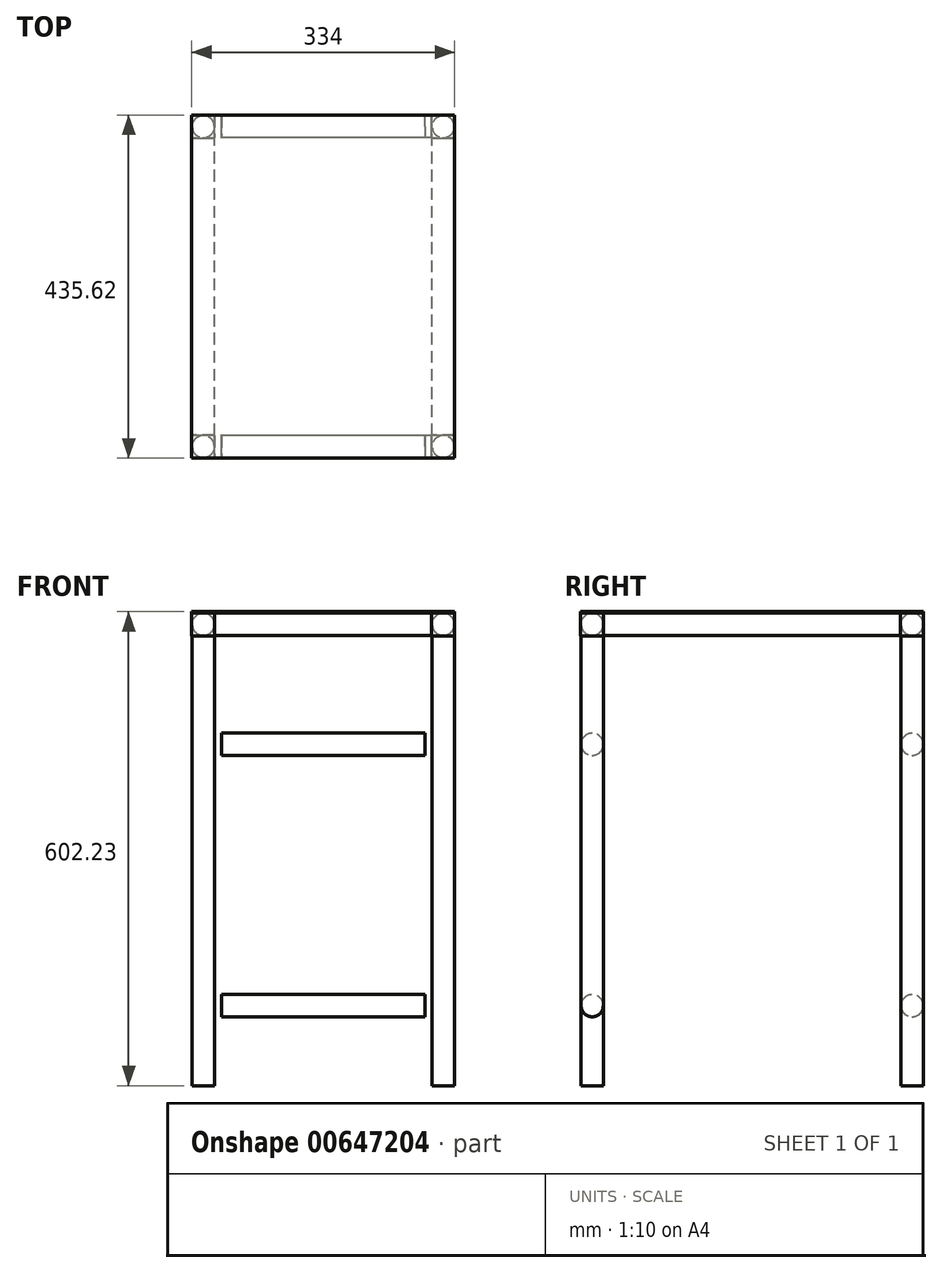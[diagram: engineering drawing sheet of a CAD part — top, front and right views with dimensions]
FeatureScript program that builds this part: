
annotation { "Feature Type Name" : "Feature", "Feature Type Description" : "" }
export const myFeature = defineFeature(function(context is Context, id is Id, definition is map)
    precondition{}
    {
        {
            var Q0;
            Q0=qCreatedBy(makeId("Top.planeOp"),FACE);
            var sketch = newSketch(context, id + "F0", { "sketchPlane" : qUnion([Q0])});
            skCircle(sketch, "E0", {"center": v(-152.4, 203.2) * mm, "radius": 14.05 * mm});
            skCircle(sketch, "E1", {"center": v(152.4, 203.2) * mm, "radius": 14.05 * mm});
            skCircle(sketch, "E2", {"center": v(-152.4, -203.2) * mm, "radius": 14.05 * mm});
            skCircle(sketch, "E3", {"center": v(152.4, -203.2) * mm, "radius": 14.05 * mm});
            skLineSegment(sketch, "E4", {"start": v(-152.4, 203.2) * mm, "end": v(152.4, 203.2) * mm, "construction": true});
            skLineSegment(sketch, "E5", {"start": v(-152.4, 203.2) * mm, "end": v(-152.4, -203.2) * mm, "construction": true});
            skLineSegment(sketch, "E6", {"start": v(-152.4, -203.2) * mm, "end": v(152.4, -203.2) * mm, "construction": true});
            skLineSegment(sketch, "E7", {"start": v(152.4, 203.2) * mm, "end": v(152.4, -203.2) * mm, "construction": true});
            skSolve(sketch);
        }
        {
            var Q0;
            Q0 = qSketchRegion(id + "F0", true);
            extrude(context, id + "F1", {"entities" : qUnion([Q0]), "depth" : 571.5 * mm, "offsetDistance" : 25.4 * mm});
        }
        {
            var Q0;
            Q0=qCreatedBy(makeId("Right.planeOp"),FACE);
            var sketch = newSketch(context, id + "F2", { "sketchPlane" : qUnion([Q0])});
            skLineSegment(sketch, "E8.bottom", {"start": v(-203.2, 101.6) * mm, "end": v(203.2, 101.6) * mm, "construction": true});
            skLineSegment(sketch, "E8.left", {"start": v(-203.2, 101.6) * mm, "end": v(-203.2, 433.7) * mm, "construction": true});
            skLineSegment(sketch, "E8.right", {"start": v(203.2, 101.6) * mm, "end": v(203.2, 433.7) * mm, "construction": true});
            skPoint(sketch, "E8.middle", {"position": v(0, 267.65) * mm});
            skLineSegment(sketch, "E9.bottom", {"start": v(-203.2, 433.7) * mm, "end": v(203.2, 433.7) * mm, "construction": true});
            skLineSegment(sketch, "E9.top", {"start": v(-203.2, 586.1) * mm, "end": v(203.2, 586.1) * mm, "construction": true});
            skLineSegment(sketch, "E9.left", {"start": v(-203.2, 433.7) * mm, "end": v(-203.2, 586.1) * mm, "construction": true});
            skLineSegment(sketch, "E9.right", {"start": v(203.2, 433.7) * mm, "end": v(203.2, 586.1) * mm, "construction": true});
            skPoint(sketch, "E9.middle", {"position": v(0, 509.9) * mm});
            skCircle(sketch, "E10", {"center": v(203.2, 101.6) * mm, "radius": 14.05 * mm});
            skCircle(sketch, "E11", {"center": v(203.2, 433.7) * mm, "radius": 14.05 * mm});
            skCircle(sketch, "E12", {"center": v(203.2, 586.1) * mm, "radius": 14.05 * mm});
            skCircle(sketch, "E13", {"center": v(-203.2, 586.1) * mm, "radius": 14.05 * mm});
            skCircle(sketch, "E14", {"center": v(-203.2, 433.7) * mm, "radius": 14.05 * mm});
            skCircle(sketch, "E15", {"center": v(-203.2, 101.6) * mm, "radius": 14.05 * mm});
            skSolve(sketch);
        }
        {
            var Q0;
            Q0 = qSketchRegion(id + "F2", true);
            extrude(context, id + "F3", {"entities" : qUnion([Q0]), "endBound" : BoundingType.SYMMETRIC, "depth" : 275.59 * mm, "offsetDistance" : 25.4 * mm});
        }
        {
            var Q0;
            Q0=makeQuery(id+"F1.opExtrude","CAP_FACE",FACE,{"disambiguationData":[OSD([sQuery(id+"F0.wireOp",EDGE,"E3")])],"isStart":false});
            var sketch = newSketch(context, id + "F4", { "sketchPlane" : qUnion([Q0])});
            skLineSegment(sketch, "E16.bottom", {"start": v(167, -217.8) * mm, "end": v(137.8, -217.8) * mm});
            skLineSegment(sketch, "E16.top", {"start": v(167, -188.6) * mm, "end": v(137.8, -188.6) * mm});
            skLineSegment(sketch, "E16.left", {"start": v(167, -217.8) * mm, "end": v(167, -188.6) * mm});
            skLineSegment(sketch, "E16.right", {"start": v(137.8, -217.8) * mm, "end": v(137.8, -188.6) * mm});
            skPoint(sketch, "E16.middle", {"position": v(152.4, -203.2) * mm});
            skLineSegment(sketch, "E17.bottom", {"start": v(167, 188.6) * mm, "end": v(137.8, 188.6) * mm});
            skLineSegment(sketch, "E17.top", {"start": v(167, 217.8) * mm, "end": v(137.8, 217.8) * mm});
            skLineSegment(sketch, "E17.left", {"start": v(167, 188.6) * mm, "end": v(167, 217.8) * mm});
            skLineSegment(sketch, "E17.right", {"start": v(137.8, 188.6) * mm, "end": v(137.8, 217.8) * mm});
            skPoint(sketch, "E17.middle", {"position": v(152.4, 203.2) * mm});
            skLineSegment(sketch, "E18.bottom", {"start": v(-137.8, 188.6) * mm, "end": v(-167, 188.6) * mm});
            skLineSegment(sketch, "E18.top", {"start": v(-137.8, 217.8) * mm, "end": v(-167, 217.8) * mm});
            skLineSegment(sketch, "E18.left", {"start": v(-137.8, 188.6) * mm, "end": v(-137.8, 217.8) * mm});
            skLineSegment(sketch, "E18.right", {"start": v(-167, 188.6) * mm, "end": v(-167, 217.8) * mm});
            skPoint(sketch, "E18.middle", {"position": v(-152.4, 203.2) * mm});
            skLineSegment(sketch, "E19.bottom", {"start": v(-137.8, -217.8) * mm, "end": v(-167, -217.8) * mm});
            skLineSegment(sketch, "E19.top", {"start": v(-137.8, -188.6) * mm, "end": v(-167, -188.6) * mm});
            skLineSegment(sketch, "E19.left", {"start": v(-137.8, -217.8) * mm, "end": v(-137.8, -188.6) * mm});
            skLineSegment(sketch, "E19.right", {"start": v(-167, -217.8) * mm, "end": v(-167, -188.6) * mm});
            skPoint(sketch, "E19.middle", {"position": v(-152.4, -203.2) * mm});
            skSolve(sketch);
        }
        {
            var Q0;
            Q0 = qSketchRegion(id + "F4", true);
            extrude(context, id + "F5", {"entities" : qUnion([Q0]), "depth" : 29.2 * mm, "offsetDistance" : 25.4 * mm});
        }
        {
            var Q0;
            Q0=makeQuery(id+"F3.opExtrude","CAP_FACE",FACE,{"disambiguationData":[OSD([sQuery(id+"F2.wireOp",EDGE,"E14")])],"isStart":false});
            var sketch = newSketch(context, id + "F6", { "sketchPlane" : qUnion([Q0])});
            skCircle(sketch, "E20.0", {"center": v(-203.2, 433.7) * mm, "radius": 14.05 * mm});
            skCircle(sketch, "E21.0.0", {"center": v(203.2, 433.7) * mm, "radius": 14.05 * mm});
            skCircle(sketch, "E22.0.0", {"center": v(-203.2, 101.6) * mm, "radius": 14.05 * mm});
            skCircle(sketch, "E23.0.0", {"center": v(203.2, 101.6) * mm, "radius": 14.05 * mm});
            skSolve(sketch);
        }
        {
            var Q0;
            Q0 = qSketchRegion(id + "F6", true);
            extrude(context, id + "F7", {"entities" : qUnion([Q0]), "operationType" : NewBodyOperationType.REMOVE, "oppositeDirection" : true, "depth" : 8.5 * mm, "offsetDistance" : 25.4 * mm});
        }
        {
            var Q0;
            Q0=makeQuery(id+"F3.opExtrude","CAP_FACE",FACE,{"disambiguationData":[OSD([sQuery(id+"F2.wireOp",EDGE,"E15")])],"isStart":true});
            var sketch = newSketch(context, id + "F8", { "sketchPlane" : qUnion([Q0])});
            skCircle(sketch, "E24.0", {"center": v(203.2, 101.6) * mm, "radius": 14.05 * mm});
            skCircle(sketch, "E25.0", {"center": v(203.2, 433.7) * mm, "radius": 14.05 * mm});
            skCircle(sketch, "E26.0", {"center": v(-203.2, 433.7) * mm, "radius": 14.05 * mm});
            skCircle(sketch, "E27.0", {"center": v(-203.2, 101.6) * mm, "radius": 14.05 * mm});
            skSolve(sketch);
        }
        {
            var Q0;
            Q0 = qSketchRegion(id + "F8", true);
            extrude(context, id + "F9", {"entities" : qUnion([Q0]), "operationType" : NewBodyOperationType.REMOVE, "oppositeDirection" : true, "depth" : 8.5 * mm, "offsetDistance" : 25.4 * mm});
        }
        {
            var Q0;
            Q0=makeQuery(id+"F5.opExtrude","SWEPT_FACE",FACE,{"disambiguationData":[OSD([sQuery(id+"F4.wireOp",EDGE,"E17.bottom")])]});
            var sketch = newSketch(context, id + "F10", { "sketchPlane" : qUnion([Q0])});
            skCircle(sketch, "E28", {"center": v(152.4, 586.1) * mm, "radius": 14.05 * mm});
            skCircle(sketch, "E29", {"center": v(-152.4, 586.1) * mm, "radius": 14.05 * mm});
            skLineSegment(sketch, "E30", {"start": v(152.4, 571.5) * mm, "end": v(152.4, 600.7) * mm, "construction": true});
            skLineSegment(sketch, "E31", {"start": v(-152.4, 600.7) * mm, "end": v(-152.4, 571.5) * mm, "construction": true});
            skSolve(sketch);
        }
        {
            var Q0;
            Q0 = qSketchRegion(id + "F10", true);
            extrude(context, id + "F11", {"entities" : qUnion([Q0]), "endBound" : BoundingType.UP_TO_NEXT, "depth" : 25.4 * mm, "offsetDistance" : 25.4 * mm});
        }
        {
            var Q0;
            Q0=makeQuery(id+"F5.opExtrude","CAP_FACE",FACE,{"disambiguationData":[OSD([sQuery(id+"F4.wireOp",EDGE,"E16.bottom"),sQuery(id+"F4.wireOp",EDGE,"E16.top"),sQuery(id+"F4.wireOp",EDGE,"E16.left"),sQuery(id+"F4.wireOp",EDGE,"E16.right")])],"isStart":false});
            var sketch = newSketch(context, id + "F12", { "sketchPlane" : qUnion([Q0])});
            skLineSegment(sketch, "E32.bottom", {"start": v(167, -217.8) * mm, "end": v(-167, -217.8) * mm});
            skLineSegment(sketch, "E32.top", {"start": v(167, 217.8) * mm, "end": v(-167, 217.8) * mm});
            skLineSegment(sketch, "E32.left", {"start": v(167, -217.8) * mm, "end": v(167, 217.8) * mm});
            skLineSegment(sketch, "E32.right", {"start": v(-167, -217.8) * mm, "end": v(-167, 217.8) * mm});
            skSolve(sketch);
        }
        {
            var Q0;
            Q0 = qSketchRegion(id + "F12", true);
            extrude(context, id + "F13", {"entities" : qUnion([Q0]), "depth" : 1.52 * mm, "offsetDistance" : 25.4 * mm});
        }
    });
